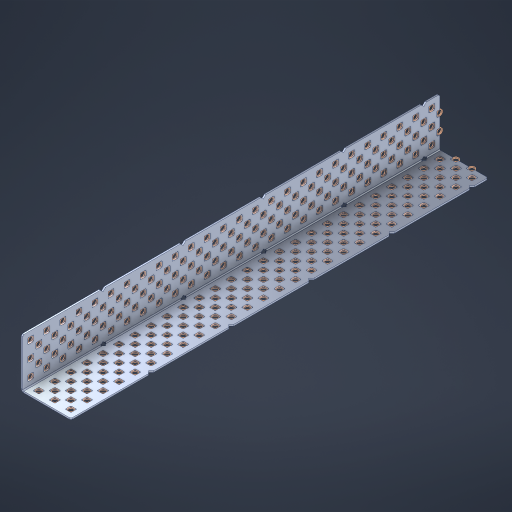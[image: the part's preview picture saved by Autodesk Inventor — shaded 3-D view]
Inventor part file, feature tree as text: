
AUTODESK INVENTOR PART (.ipt)
format: ipt  version: 2023 (Build 270158000, 158)  size: 2,701,824 bytes
history: native  units: in
note: dims shown in document units (in); Inventor stores cm internally (conversion verified against a paired STEP export)
features: other x266, extrude x258, sheet_metal_op x8, sketch x7, pattern_linear x3, mirror x1, chamfer x1
ambient origin geometry x8: Origin, YZ Plane, XZ Plane, XY Plane, X Axis, Y Axis, Z Axis, Center Point
bodies: Solid1 (feature_tree), Body (feature_tree)
feature tree (544):
  sheet_metal_op  "Flanges"
  sheet_metal_op  "Body Pattern"
  pattern_linear  "Center Double"  Spacing1=1.5in  [1 undecoded]
  pattern_linear  "Center Pattern"  Spacing1=0.1875in  [1 undecoded]
  other  "Arc Length"
  pattern_linear  "Notch Pattern"  Spacing1=0.0469in  [1 undecoded]
  other  "Diagonal Plane"
  mirror  "Everything Mirrored"
  chamfer  "End Chamfer"
  sketch  "Sketch1"  dims[d0=1.5in]
  other  "Plate1"
  sketch  "Sketch2"  dims[d1=13.0in]
  other  "Plate2"
  sheet_metal_op  "Bend1"
  sheet_metal_op  "Corner1"
  sketch  "Sketch8"  dims[d2=0.0469in]
  sketch  "Sketch9"  dims[d3=0.0469in]
  other  "Srf91"
  sheet_metal_op  "Body Pattern Sketch"
  other  "Srf92"
  sketch  "Sketch13"  dims[d4=0.0234in]
  sketch  "Sketch15"  dims[d5=0.0938in]
  sketch  "Sketch16"  dims[d6=0.0469in d7=1.5in d8=90.0deg d9=0.0312in d10=0.1875in d11=0.0469in d12=0.0469in d49=0.182in d50=0.02in d52=0.25in d53=0.0469in d54=0.0in d55=0.172in d56=1.0in d57=0.0in d85=0.1473in d86=0.1659in d89=0.0469in d90=0.0in d91=0.04in d92=0.0491in d95=2.5in d96=0.04in d97=0.25in d98=45.0deg d106=0.182in d107=0.02in d110=0.0469in d111=0.0in d112=0.172in d113=0.5in d114=0.0in d117=0.5in d126=0.0491in d127=0.1227in d128=0.08in d129=0.04in d130=2.5in d131=0.25in d132=10.2362in d134=0.5in d135=1.1811in d137=0.5in d140=0.5in d141=1.0in d142=0.3937in d144=0.5in d145=0.071in d146=0.7874in d148=0.5in]
  other  "Srf786"
  other  "Srf856"
  other  "Srf889"
  other  "Srf890"
  other  "Srf891"
  other  "Srf1275"
  other  "Srf1276"
  other  "Srf1278"
  other  "Srf1277"
  other  "Srf1285"
  other  "Srf1286"
  other  "Srf1287"
  other  "Srf1445"
  other  "Srf1446"
  other  "Srf1447"
  other  "Srf1448"
  other  "Srf1449"
  other  "Srf1537"
  other  "Srf1538"
  other  "Srf1539"
  other  "Srf1540"
  other  "Srf1541"
  other  "Srf1807"
  other  "Srf1808"
  other  "Srf1809"
  other  "Srf1810"
  other  "Srf1811"
  other  "Srf1812"
  other  "Srf1813"
  other  "Srf1814"
  other  "Srf1815"
  other  "Srf1816"
  other  "Srf1817"
  other  "Srf1818"
  other  "Srf1819"
  other  "Srf1820"
  other  "Srf1821"
  other  "Srf1822"
  other  "Srf1823"
  other  "Srf1959"
  other  "Srf1960"
  other  "Srf1961"
  other  "Srf1962"
  other  "Srf1963"
  other  "Srf1964"
  other  "Srf1965"
  other  "Srf1966"
  other  "Srf1967"
  other  "Srf1968"
  other  "Srf1969"
  other  "Srf1970"
  other  "Srf1971"
  other  "Srf1972"
  other  "Srf1973"
  other  "Srf1974"
  other  "Srf1975"
  other  "Srf2009"
  other  "Srf2010"
  other  "Srf2011"
  other  "Srf2012"
  other  "Srf2013"
  other  "Srf2014"
  other  "Srf2015"
  other  "Srf2016"
  other  "Srf2017"
  other  "Srf2018"
  other  "Srf2019"
  other  "Srf2020"
  other  "Srf2021"
  other  "Srf2022"
  other  "Srf2023"
  other  "Srf2024"
  other  "Srf2025"
  other  "Srf2026"
  other  "Srf2027"
  other  "Srf2028"
  other  "Srf2029"
  other  "Srf2030"
  other  "Srf2031"
  other  "Srf2032"
  other  "Srf2033"
  other  "Srf2034"
  other  "Srf2043"
  other  "Srf2044"
  other  "Srf2045"
  other  "Srf2046"
  other  "Srf2047"
  other  "Srf2048"
  other  "Srf2049"
  other  "Srf2050"
  other  "Srf2051"
  other  "Srf2052"
  other  "Srf2053"
  other  "Srf2054"
  other  "Srf2055"
  other  "Srf2056"
  other  "Srf2057"
  other  "Srf2058"
  other  "Srf2059"
  other  "Srf2060"
  other  "Srf2061"
  other  "Srf2062"
  other  "Srf2063"
  other  "Srf2064"
  other  "Srf2065"
  other  "Srf2066"
  other  "Srf2067"
  other  "Srf2076"
  other  "Srf2077"
  other  "Srf2078"
  other  "Srf2079"
  other  "Srf2080"
  other  "Srf2081"
  other  "Srf2082"
  other  "Srf2083"
  other  "Srf2084"
  other  "Srf2085"
  other  "Srf2086"
  other  "Srf2087"
  other  "Srf2088"
  other  "Srf2089"
  other  "Srf2090"
  other  "Srf2091"
  other  "Srf2092"
  other  "Srf2093"
  other  "Srf2094"
  other  "Srf2095"
  other  "Srf2096"
  other  "Srf2097"
  other  "Srf2098"
  other  "Srf2099"
  other  "Srf2100"
  other  "Srf2101"
  other  "Srf2102"
  other  "Srf2103"
  other  "Srf2104"
  other  "Srf2105"
  other  "Srf2106"
  other  "Srf2107"
  other  "Srf2108"
  other  "Srf2109"
  other  "Srf2110"
  other  "Srf2111"
  other  "Srf2112"
  other  "Srf2113"
  other  "Srf2114"
  other  "Srf2115"
  other  "Srf2116"
  other  "Srf2117"
  other  "Srf2118"
  other  "Srf2119"
  other  "Srf2120"
  other  "Srf2121"
  other  "Srf2122"
  other  "Srf2123"
  other  "Srf2124"
  other  "Srf2125"
  other  "Srf2126"
  other  "Srf2127"
  other  "Srf2128"
  other  "Srf2129"
  other  "Srf2130"
  other  "Srf2131"
  other  "Srf2132"
  other  "Srf2133"
  other  "Srf2134"
  other  "Srf2135"
  other  "Srf2136"
  other  "Srf2137"
  other  "Srf2138"
  other  "Srf2139"
  other  "Srf2140"
  other  "Srf2141"
  other  "Srf2142"
  other  "Srf2143"
  other  "Srf2144"
  other  "Srf2145"
  other  "Srf2146"
  other  "Srf2147"
  other  "Srf2148"
  other  "Srf2149"
  other  "Srf2150"
  other  "Srf2151"
  other  "Srf2179"
  other  "Srf2180"
  other  "Srf2181"
  other  "Srf2182"
  other  "Srf2183"
  other  "Srf2184"
  other  "Srf2185"
  other  "Srf2186"
  other  "Srf2187"
  other  "Srf2188"
  other  "Srf2189"
  other  "Srf2190"
  other  "Srf2191"
  other  "Srf2192"
  other  "Srf2193"
  other  "Srf2194"
  other  "Srf2195"
  other  "Srf2196"
  other  "Srf2197"
  other  "Srf2198"
  other  "Srf2199"
  other  "Srf2200"
  other  "Srf2201"
  other  "Srf2202"
  other  "Srf2203"
  other  "Srf2204"
  other  "Srf2205"
  other  "Srf2206"
  other  "Srf2207"
  other  "Srf2208"
  other  "Srf2209"
  other  "Srf2210"
  other  "Srf2211"
  other  "Srf2212"
  other  "Srf2213"
  other  "Srf2214"
  other  "Srf2215"
  other  "Srf2216"
  other  "Srf2217"
  other  "Srf2218"
  other  "Srf2219"
  other  "Srf2220"
  other  "Srf2221"
  other  "Srf2222"
  other  "Srf2223"
  other  "Srf2224"
  other  "Srf2225"
  other  "Srf2226"
  other  "Srf2227"
  other  "Srf2228"
  other  "Srf2229"
  other  "Srf2230"
  other  "Srf2231"
  other  "Srf2232"
  other  "Srf2233"
  other  "Srf2234"
  other  "Srf2235"
  other  "Srf2236"
  other  "Srf2237"
  other  "Srf2238"
  other  "Srf2239"
  other  "Srf2240"
  other  "Srf2241"
  other  "Srf2242"
  other  "Srf2243"
  other  "Srf2244"
  other  "Srf2245"
  other  "Srf2246"
  other  "Srf2247"
  other  "Srf2248"
  other  "Srf2249"
  other  "Srf2250"
  other  "Srf2251"
  other  "Srf2252"
  other  "Srf2253"
  sheet_metal_op  "Body Stamp"
  sheet_metal_op  "Body Circle"
  other  "Center Stamp"
  other  "Center Circle"
  sheet_metal_op  "Notch"
  extrude  "ExtrusionSrf92"  Depth=0.0469in
  extrude  "ExtrusionSrf856"  Depth=0.182in
  extrude  "ExtrusionSrf889"  Depth=0.02in
  extrude  "ExtrusionSrf890"  Depth=0.25in
  extrude  "ExtrusionSrf891"  Depth=0.0469in
  extrude  "ExtrusionSrf1275"  TaperAngle=0.0deg  [1 undecoded]
  extrude  "ExtrusionSrf1276"  Depth=0.5in
  extrude  "ExtrusionSrf1277"  Depth=1.0in TaperAngle=0.0deg
  extrude  "ExtrusionSrf1345"  Depth=0.5in
  extrude  "ExtrusionSrf1346"  Depth=0.5in
  extrude  "ExtrusionSrf1347"  Depth=0.0469in
  extrude  "ExtrusionSrf1348"  Depth=0.5in TaperAngle=0.0deg
  extrude  "ExtrusionSrf1445"  Depth=0.5in
  extrude  "ExtrusionSrf1446"  Depth=0.25in TaperAngle=45.0deg
  extrude  "ExtrusionSrf1447"  Depth=0.182in
  extrude  "ExtrusionSrf1448"  Depth=0.02in
  extrude  "ExtrusionSrf1449"  Depth=0.0469in
  extrude  "ExtrusionSrf1537"  TaperAngle=0.0deg  [1 undecoded]
  extrude  "ExtrusionSrf1538"  Depth=0.5in
  extrude  "ExtrusionSrf1539"  Depth=0.5in TaperAngle=0.0deg
  extrude  "ExtrusionSrf1540"  Depth=0.5in
  extrude  "ExtrusionSrf1541"  Depth=0.5in
  extrude  "ExtrusionSrf1807"  Depth=0.5in
  extrude  "ExtrusionSrf1808"  Depth=0.5in
  extrude  "ExtrusionSrf1809"  Depth=0.5in
  extrude  "ExtrusionSrf1810"  Depth=0.5in
  extrude  "ExtrusionSrf1811"  Depth=0.25in
  extrude  "ExtrusionSrf1812"  Depth=0.5in
  extrude  "ExtrusionSrf1813"  Depth=0.5in
  extrude  "ExtrusionSrf1814"  Depth=0.5in
  extrude  "ExtrusionSrf1815"  Depth=1.0in
  extrude  "ExtrusionSrf1816"  Depth=0.3937in
  extrude  "ExtrusionSrf1817"  Depth=0.5in
  extrude  "ExtrusionSrf1818"  Depth=0.5in
  extrude  "ExtrusionSrf1819"  [1 undecoded]
  extrude  "ExtrusionSrf1820"  [1 undecoded]
  extrude  "ExtrusionSrf1821"  [1 undecoded]
  extrude  "ExtrusionSrf1822"  [1 undecoded]
  extrude  "ExtrusionSrf1823"  [1 undecoded]
  extrude  "ExtrusionSrf1959"  [1 undecoded]
  extrude  "ExtrusionSrf1960"  [1 undecoded]
  extrude  "ExtrusionSrf1961"  [1 undecoded]
  extrude  "ExtrusionSrf1962"  [1 undecoded]
  extrude  "ExtrusionSrf1963"  [1 undecoded]
  extrude  "ExtrusionSrf1964"  [1 undecoded]
  extrude  "ExtrusionSrf1965"  [1 undecoded]
  extrude  "ExtrusionSrf1966"  [1 undecoded]
  extrude  "ExtrusionSrf1967"  [1 undecoded]
  extrude  "ExtrusionSrf1968"  [1 undecoded]
  extrude  "ExtrusionSrf1969"  [1 undecoded]
  extrude  "ExtrusionSrf1970"  [1 undecoded]
  extrude  "ExtrusionSrf1971"  [1 undecoded]
  extrude  "ExtrusionSrf1972"  [1 undecoded]
  extrude  "ExtrusionSrf1973"  [1 undecoded]
  extrude  "ExtrusionSrf1974"  [1 undecoded]
  extrude  "ExtrusionSrf1975"  [1 undecoded]
  extrude  "ExtrusionSrf2009"  [1 undecoded]
  extrude  "ExtrusionSrf2010"  [1 undecoded]
  extrude  "ExtrusionSrf2011"  [1 undecoded]
  extrude  "ExtrusionSrf2012"  [1 undecoded]
  extrude  "ExtrusionSrf2013"  [1 undecoded]
  extrude  "ExtrusionSrf2014"  [1 undecoded]
  extrude  "ExtrusionSrf2015"  [1 undecoded]
  extrude  "ExtrusionSrf2016"  [1 undecoded]
  extrude  "ExtrusionSrf2017"  [1 undecoded]
  extrude  "ExtrusionSrf2018"  [1 undecoded]
  extrude  "ExtrusionSrf2019"  [1 undecoded]
  extrude  "ExtrusionSrf2020"  [1 undecoded]
  extrude  "ExtrusionSrf2021"  [1 undecoded]
  extrude  "ExtrusionSrf2022"  [1 undecoded]
  extrude  "ExtrusionSrf2023"  [1 undecoded]
  extrude  "ExtrusionSrf2024"  [1 undecoded]
  extrude  "ExtrusionSrf2025"  [1 undecoded]
  extrude  "ExtrusionSrf2026"  [1 undecoded]
  extrude  "ExtrusionSrf2027"  [1 undecoded]
  extrude  "ExtrusionSrf2028"  [1 undecoded]
  extrude  "ExtrusionSrf2029"  [1 undecoded]
  extrude  "ExtrusionSrf2030"  [1 undecoded]
  extrude  "ExtrusionSrf2031"  [1 undecoded]
  extrude  "ExtrusionSrf2032"  [1 undecoded]
  extrude  "ExtrusionSrf2033"  [1 undecoded]
  extrude  "ExtrusionSrf2034"  [1 undecoded]
  extrude  "ExtrusionSrf2043"  [1 undecoded]
  extrude  "ExtrusionSrf2044"  [1 undecoded]
  extrude  "ExtrusionSrf2045"  [1 undecoded]
  extrude  "ExtrusionSrf2046"  [1 undecoded]
  extrude  "ExtrusionSrf2047"  [1 undecoded]
  extrude  "ExtrusionSrf2048"  [1 undecoded]
  extrude  "ExtrusionSrf2049"  [1 undecoded]
  extrude  "ExtrusionSrf2050"  [1 undecoded]
  extrude  "ExtrusionSrf2051"  [1 undecoded]
  extrude  "ExtrusionSrf2052"  [1 undecoded]
  extrude  "ExtrusionSrf2053"  [1 undecoded]
  extrude  "ExtrusionSrf2054"  [1 undecoded]
  extrude  "ExtrusionSrf2055"  [1 undecoded]
  extrude  "ExtrusionSrf2056"  [1 undecoded]
  extrude  "ExtrusionSrf2057"  [1 undecoded]
  extrude  "ExtrusionSrf2058"  [1 undecoded]
  extrude  "ExtrusionSrf2059"  [1 undecoded]
  extrude  "ExtrusionSrf2060"  [1 undecoded]
  extrude  "ExtrusionSrf2061"  [1 undecoded]
  extrude  "ExtrusionSrf2062"  [1 undecoded]
  extrude  "ExtrusionSrf2063"  [1 undecoded]
  extrude  "ExtrusionSrf2064"  [1 undecoded]
  extrude  "ExtrusionSrf2065"  [1 undecoded]
  extrude  "ExtrusionSrf2066"  [1 undecoded]
  extrude  "ExtrusionSrf2067"  [1 undecoded]
  extrude  "ExtrusionSrf2076"  [1 undecoded]
  extrude  "ExtrusionSrf2077"  [1 undecoded]
  extrude  "ExtrusionSrf2078"  [1 undecoded]
  extrude  "ExtrusionSrf2079"  [1 undecoded]
  extrude  "ExtrusionSrf2080"  [1 undecoded]
  extrude  "ExtrusionSrf2081"  [1 undecoded]
  extrude  "ExtrusionSrf2082"  [1 undecoded]
  extrude  "ExtrusionSrf2083"  [1 undecoded]
  extrude  "ExtrusionSrf2084"  [1 undecoded]
  extrude  "ExtrusionSrf2085"  [1 undecoded]
  extrude  "ExtrusionSrf2086"  [1 undecoded]
  extrude  "ExtrusionSrf2087"  [1 undecoded]
  extrude  "ExtrusionSrf2088"  [1 undecoded]
  extrude  "ExtrusionSrf2089"  [1 undecoded]
  extrude  "ExtrusionSrf2090"  [1 undecoded]
  extrude  "ExtrusionSrf2091"  [1 undecoded]
  extrude  "ExtrusionSrf2092"  [1 undecoded]
  extrude  "ExtrusionSrf2093"  [1 undecoded]
  extrude  "ExtrusionSrf2094"  [1 undecoded]
  extrude  "ExtrusionSrf2095"  [1 undecoded]
  extrude  "ExtrusionSrf2096"  [1 undecoded]
  extrude  "ExtrusionSrf2097"  [1 undecoded]
  extrude  "ExtrusionSrf2098"  [1 undecoded]
  extrude  "ExtrusionSrf2099"  [1 undecoded]
  extrude  "ExtrusionSrf2100"  [1 undecoded]
  extrude  "ExtrusionSrf2101"  [1 undecoded]
  extrude  "ExtrusionSrf2102"  [1 undecoded]
  extrude  "ExtrusionSrf2103"  [1 undecoded]
  extrude  "ExtrusionSrf2104"  [1 undecoded]
  extrude  "ExtrusionSrf2105"  [1 undecoded]
  extrude  "ExtrusionSrf2106"  [1 undecoded]
  extrude  "ExtrusionSrf2107"  [1 undecoded]
  extrude  "ExtrusionSrf2108"  [1 undecoded]
  extrude  "ExtrusionSrf2109"  [1 undecoded]
  extrude  "ExtrusionSrf2110"  [1 undecoded]
  extrude  "ExtrusionSrf2111"  [1 undecoded]
  extrude  "ExtrusionSrf2112"  [1 undecoded]
  extrude  "ExtrusionSrf2113"  [1 undecoded]
  extrude  "ExtrusionSrf2114"  [1 undecoded]
  extrude  "ExtrusionSrf2115"  [1 undecoded]
  extrude  "ExtrusionSrf2116"  [1 undecoded]
  extrude  "ExtrusionSrf2117"  [1 undecoded]
  extrude  "ExtrusionSrf2118"  [1 undecoded]
  extrude  "ExtrusionSrf2119"  [1 undecoded]
  extrude  "ExtrusionSrf2120"  [1 undecoded]
  extrude  "ExtrusionSrf2121"  [1 undecoded]
  extrude  "ExtrusionSrf2122"  [1 undecoded]
  extrude  "ExtrusionSrf2123"  [1 undecoded]
  extrude  "ExtrusionSrf2124"  [1 undecoded]
  extrude  "ExtrusionSrf2125"  [1 undecoded]
  extrude  "ExtrusionSrf2126"  [1 undecoded]
  extrude  "ExtrusionSrf2127"  [1 undecoded]
  extrude  "ExtrusionSrf2128"  [1 undecoded]
  extrude  "ExtrusionSrf2129"  [1 undecoded]
  extrude  "ExtrusionSrf2130"  [1 undecoded]
  extrude  "ExtrusionSrf2131"  [1 undecoded]
  extrude  "ExtrusionSrf2132"  [1 undecoded]
  extrude  "ExtrusionSrf2133"  [1 undecoded]
  extrude  "ExtrusionSrf2134"  [1 undecoded]
  extrude  "ExtrusionSrf2135"  [1 undecoded]
  extrude  "ExtrusionSrf2136"  [1 undecoded]
  extrude  "ExtrusionSrf2137"  [1 undecoded]
  extrude  "ExtrusionSrf2138"  [1 undecoded]
  extrude  "ExtrusionSrf2139"  [1 undecoded]
  extrude  "ExtrusionSrf2140"  [1 undecoded]
  extrude  "ExtrusionSrf2141"  [1 undecoded]
  extrude  "ExtrusionSrf2142"  [1 undecoded]
  extrude  "ExtrusionSrf2143"  [1 undecoded]
  extrude  "ExtrusionSrf2144"  [1 undecoded]
  extrude  "ExtrusionSrf2145"  [1 undecoded]
  extrude  "ExtrusionSrf2146"  [1 undecoded]
  extrude  "ExtrusionSrf2147"  [1 undecoded]
  extrude  "ExtrusionSrf2148"  [1 undecoded]
  extrude  "ExtrusionSrf2149"  [1 undecoded]
  extrude  "ExtrusionSrf2150"  [1 undecoded]
  extrude  "ExtrusionSrf2151"  [1 undecoded]
  extrude  "ExtrusionSrf2179"  [1 undecoded]
  extrude  "ExtrusionSrf2180"  [1 undecoded]
  extrude  "ExtrusionSrf2181"  [1 undecoded]
  extrude  "ExtrusionSrf2182"  [1 undecoded]
  extrude  "ExtrusionSrf2183"  [1 undecoded]
  extrude  "ExtrusionSrf2184"  [1 undecoded]
  extrude  "ExtrusionSrf2185"  [1 undecoded]
  extrude  "ExtrusionSrf2186"  [1 undecoded]
  extrude  "ExtrusionSrf2187"  [1 undecoded]
  extrude  "ExtrusionSrf2188"  [1 undecoded]
  extrude  "ExtrusionSrf2189"  [1 undecoded]
  extrude  "ExtrusionSrf2190"  [1 undecoded]
  extrude  "ExtrusionSrf2191"  [1 undecoded]
  extrude  "ExtrusionSrf2192"  [1 undecoded]
  extrude  "ExtrusionSrf2193"  [1 undecoded]
  extrude  "ExtrusionSrf2194"  [1 undecoded]
  extrude  "ExtrusionSrf2195"  [1 undecoded]
  extrude  "ExtrusionSrf2196"  [1 undecoded]
  extrude  "ExtrusionSrf2197"  [1 undecoded]
  extrude  "ExtrusionSrf2198"  [1 undecoded]
  extrude  "ExtrusionSrf2199"  [1 undecoded]
  extrude  "ExtrusionSrf2200"  [1 undecoded]
  extrude  "ExtrusionSrf2201"  [1 undecoded]
  extrude  "ExtrusionSrf2202"  [1 undecoded]
  extrude  "ExtrusionSrf2203"  [1 undecoded]
  extrude  "ExtrusionSrf2204"  [1 undecoded]
  extrude  "ExtrusionSrf2205"  [1 undecoded]
  extrude  "ExtrusionSrf2206"  [1 undecoded]
  extrude  "ExtrusionSrf2207"  [1 undecoded]
  extrude  "ExtrusionSrf2208"  [1 undecoded]
  extrude  "ExtrusionSrf2209"  [1 undecoded]
  extrude  "ExtrusionSrf2210"  [1 undecoded]
  extrude  "ExtrusionSrf2211"  [1 undecoded]
  extrude  "ExtrusionSrf2212"  [1 undecoded]
  extrude  "ExtrusionSrf2213"  [1 undecoded]
  extrude  "ExtrusionSrf2214"  [1 undecoded]
  extrude  "ExtrusionSrf2215"  [1 undecoded]
  extrude  "ExtrusionSrf2216"  [1 undecoded]
  extrude  "ExtrusionSrf2217"  [1 undecoded]
  extrude  "ExtrusionSrf2218"  [1 undecoded]
  extrude  "ExtrusionSrf2219"  [1 undecoded]
  extrude  "ExtrusionSrf2220"  [1 undecoded]
  extrude  "ExtrusionSrf2221"  [1 undecoded]
  extrude  "ExtrusionSrf2222"  [1 undecoded]
  extrude  "ExtrusionSrf2223"  [1 undecoded]
  extrude  "ExtrusionSrf2224"  [1 undecoded]
  extrude  "ExtrusionSrf2225"  [1 undecoded]
  extrude  "ExtrusionSrf2226"  [1 undecoded]
  extrude  "ExtrusionSrf2227"  [1 undecoded]
  extrude  "ExtrusionSrf2228"  [1 undecoded]
  extrude  "ExtrusionSrf2229"  [1 undecoded]
  extrude  "ExtrusionSrf2230"  [1 undecoded]
  extrude  "ExtrusionSrf2231"  [1 undecoded]
  extrude  "ExtrusionSrf2232"  [1 undecoded]
  extrude  "ExtrusionSrf2233"  [1 undecoded]
  extrude  "ExtrusionSrf2234"  [1 undecoded]
  extrude  "ExtrusionSrf2235"  [1 undecoded]
  extrude  "ExtrusionSrf2236"  [1 undecoded]
  extrude  "ExtrusionSrf2237"  [1 undecoded]
  extrude  "ExtrusionSrf2238"  [1 undecoded]
  extrude  "ExtrusionSrf2239"  [1 undecoded]
  extrude  "ExtrusionSrf2240"  [1 undecoded]
  extrude  "ExtrusionSrf2241"  [1 undecoded]
  extrude  "ExtrusionSrf2242"  [1 undecoded]
  extrude  "ExtrusionSrf2243"  [1 undecoded]
  extrude  "ExtrusionSrf2244"  [1 undecoded]
  extrude  "ExtrusionSrf2245"  [1 undecoded]
  extrude  "ExtrusionSrf2246"  [1 undecoded]
  extrude  "ExtrusionSrf2247"  [1 undecoded]
  extrude  "ExtrusionSrf2248"  [1 undecoded]
  extrude  "ExtrusionSrf2249"  [1 undecoded]
  extrude  "ExtrusionSrf2250"  [1 undecoded]
  extrude  "ExtrusionSrf2251"  [1 undecoded]
  extrude  "ExtrusionSrf2252"  [1 undecoded]
  extrude  "ExtrusionSrf2253"  [1 undecoded]
note: 229 required parameter values undecoded (feature->parameter linkage not recoverable at this tier; creation-order binding heuristic only, values carry confidence <= 0.55)
